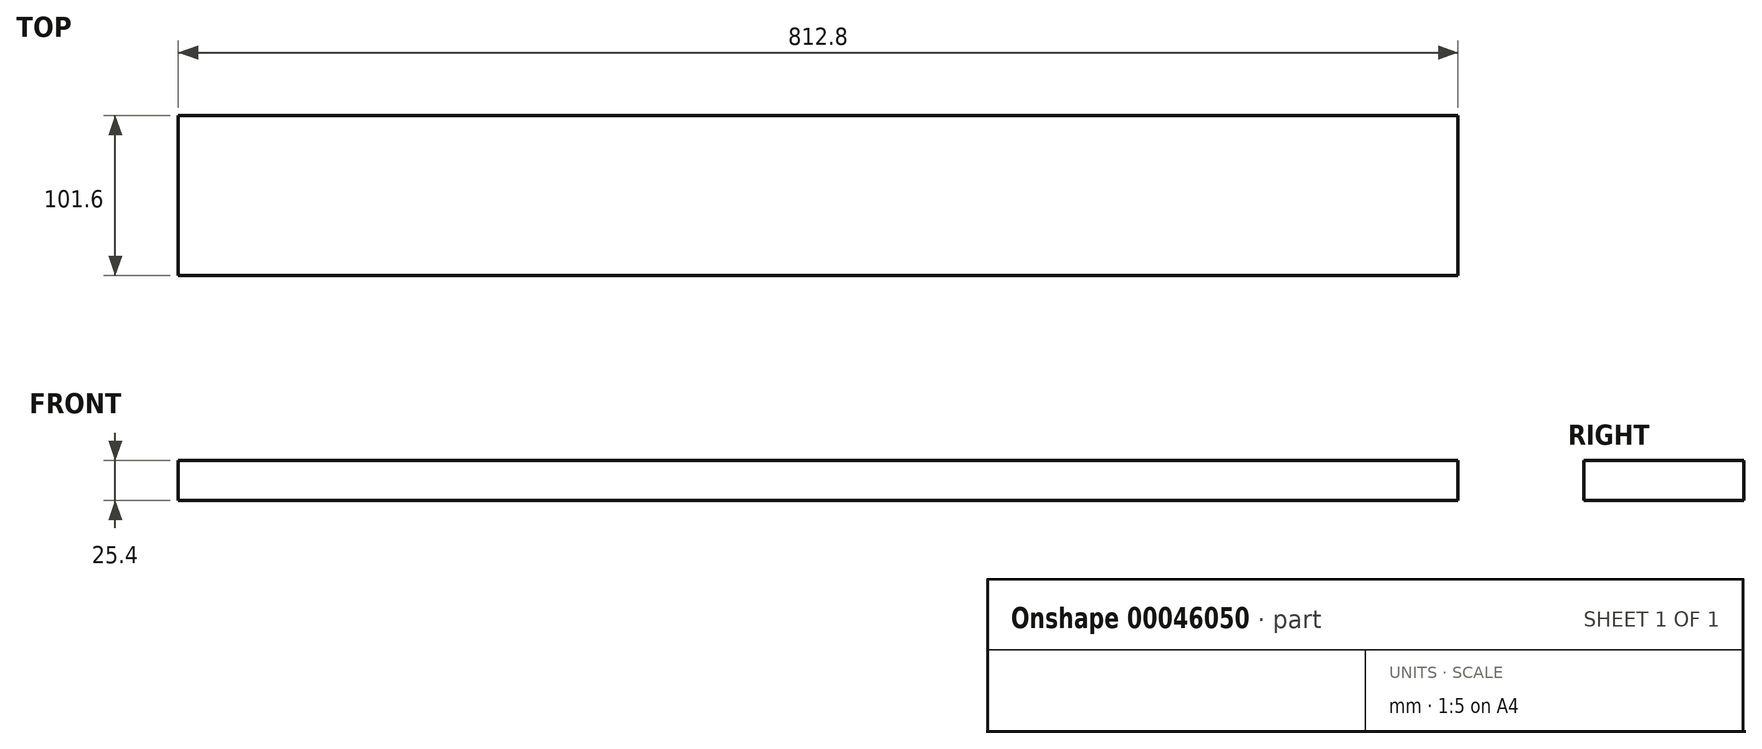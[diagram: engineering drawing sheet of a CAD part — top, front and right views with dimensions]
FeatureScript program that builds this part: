
annotation { "Feature Type Name" : "Feature", "Feature Type Description" : "" }
export const myFeature = defineFeature(function(context is Context, id is Id, definition is map)
    precondition{}
    {
        {
            var Q0;
            Q0=qCreatedBy(makeId("Top.planeOp"),FACE);
            var sketch = newSketch(context, id + "F0", { "sketchPlane" : qUnion([Q0])});
            skLineSegment(sketch, "E0.bottom", {"start": v(0, 0) * mm, "end": v(812.8, 0) * mm});
            skLineSegment(sketch, "E0.top", {"start": v(0, 101.6) * mm, "end": v(812.8, 101.6) * mm});
            skLineSegment(sketch, "E0.left", {"start": v(0, 0) * mm, "end": v(0, 101.6) * mm});
            skLineSegment(sketch, "E0.right", {"start": v(812.8, 0) * mm, "end": v(812.8, 101.6) * mm});
            skSolve(sketch);
        }
        {
            var Q0;
            Q0=makeQuery(id+"F0.imprint","IMPRINT",FACE,{"disambiguationData":[TD([[makeQuery(id+"F0.imprint","IMPRINT",EDGE,{"derivedFrom":sQuery(id+"F0.wireOp",EDGE,"E0.bottom")}),1.0]])]});
            extrude(context, id + "F1", {"entities" : qUnion([Q0]), "depth" : 25.4 * mm});
        }
    });
